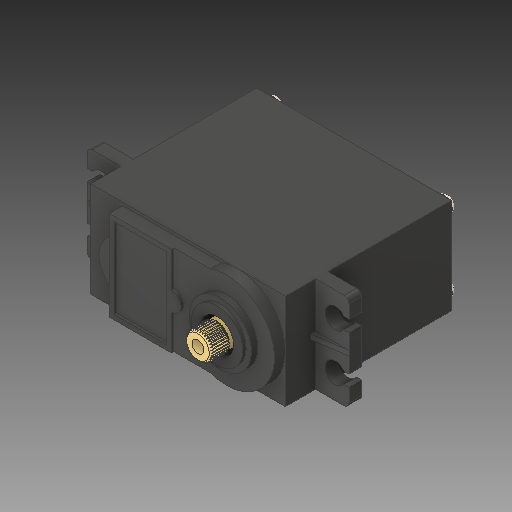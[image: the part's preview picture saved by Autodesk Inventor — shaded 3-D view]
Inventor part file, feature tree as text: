
AUTODESK INVENTOR PART (.ipt)
format: ipt  version: 2019 (Build 230136000, 136)  size: 562,176 bytes
history: mixed  units: mm
features: projected_geometry x4, other x1, sketch x1, mirror x1, imported_body x1
ambient origin geometry x8: Origin, YZ Plane, XZ Plane, XY Plane, X Axis, Y Axis, Z Axis, Center Point
bodies: Body1 (imported_parasolid)
feature tree (8):
  other  "Твердое тело1"
  sketch  "Эскиз1"
  projected_geometry  "Спроецированная петля1"
  projected_geometry  "Спроецированная петля2"
  projected_geometry  "Спроецированная петля3"
  projected_geometry  "Спроецированная петля4"
  mirror  "Mirror4"
  imported_body  NMx_Import_Brep_tag  [imported B-rep: ~118 faces, bbox_mm=[54.7, 20.0, 39.0]]
